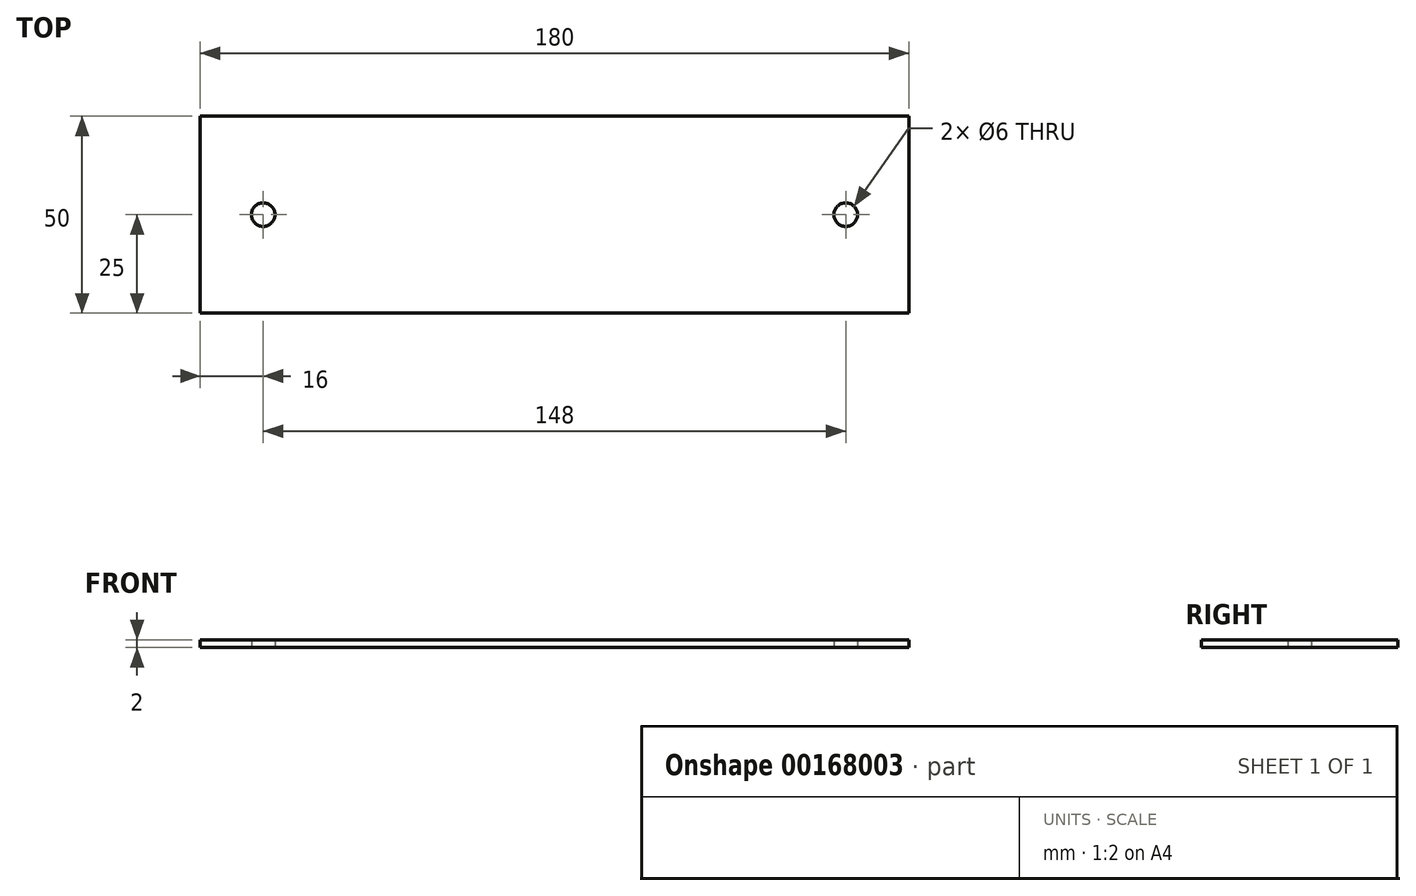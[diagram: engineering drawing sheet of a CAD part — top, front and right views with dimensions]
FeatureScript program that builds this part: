
annotation { "Feature Type Name" : "Feature", "Feature Type Description" : "" }
export const myFeature = defineFeature(function(context is Context, id is Id, definition is map)
    precondition{}
    {
        {
            var Q0;
            Q0=qCreatedBy(makeId("Top.planeOp"),FACE);
            var sketch = newSketch(context, id + "F0", { "sketchPlane" : qUnion([Q0])});
            skLineSegment(sketch, "E0.bottom", {"start": v(90, 25) * mm, "end": v(-90, 25) * mm});
            skLineSegment(sketch, "E0.top", {"start": v(90, -25) * mm, "end": v(-90, -25) * mm});
            skLineSegment(sketch, "E0.left", {"start": v(90, 25) * mm, "end": v(90, -25) * mm});
            skLineSegment(sketch, "E0.right", {"start": v(-90, 25) * mm, "end": v(-90, -25) * mm});
            skPoint(sketch, "E0.middle", {"position": v(0, 0) * mm});
            skCircle(sketch, "E1", {"center": v(-74, 0) * mm, "radius": 3 * mm});
            skPoint(sketch, "E1.centerSnap0", {"position": v(-90, 0) * mm});
            skCircle(sketch, "E2.MirrorC", {"center": v(74, 0) * mm, "radius": 3 * mm});
            skSolve(sketch);
        }
        {
            var Q0;
            Q0 = qSketchRegion(id + "F0", true);
            extrude(context, id + "F1", {"entities" : qUnion([Q0]), "depth" : 2 * mm, "symmetric" : true});
        }
    });
